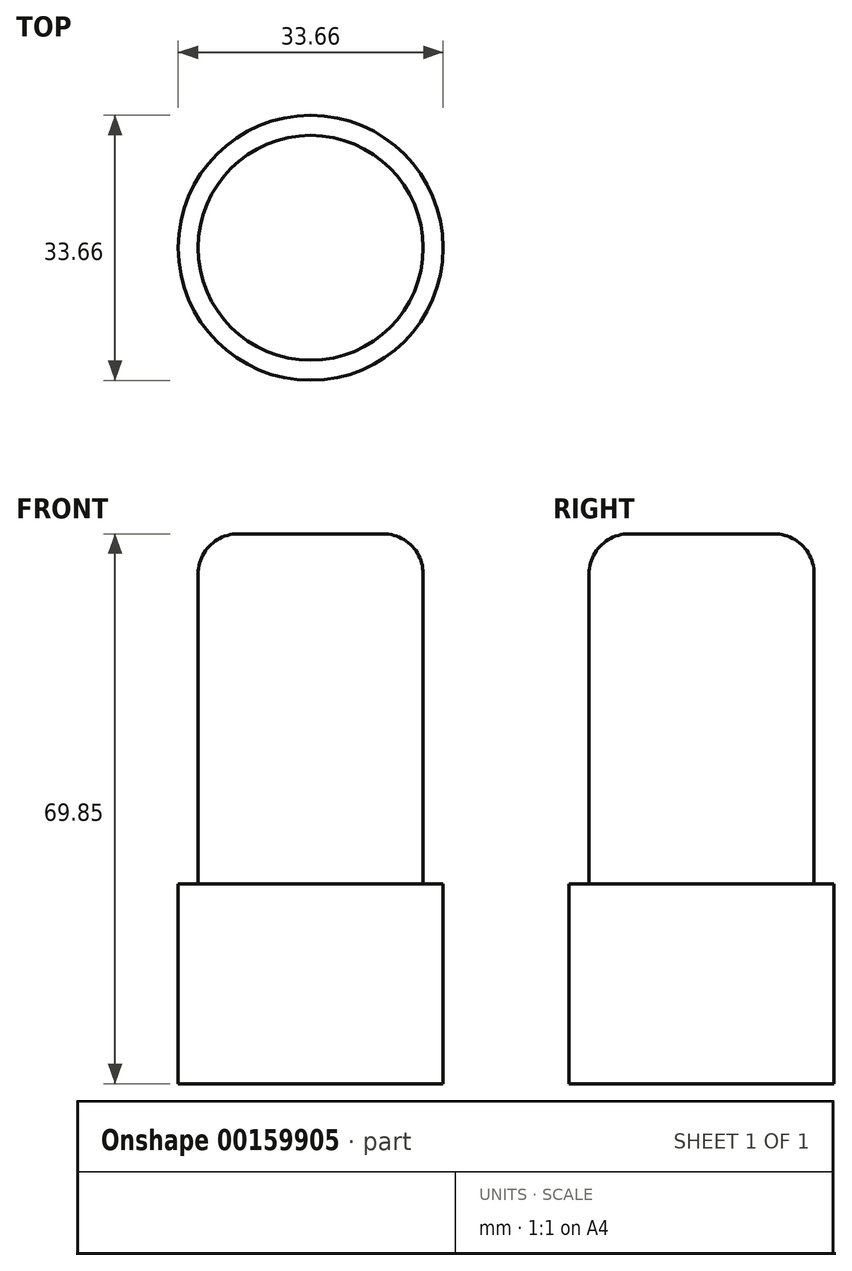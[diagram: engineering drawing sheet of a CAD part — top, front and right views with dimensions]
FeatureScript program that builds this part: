
annotation { "Feature Type Name" : "Feature", "Feature Type Description" : "" }
export const myFeature = defineFeature(function(context is Context, id is Id, definition is map)
    precondition{}
    {
        {
            var Q0;
            Q0=qCreatedBy(makeId("Top.planeOp"),FACE);
            var sketch = newSketch(context, id + "F0", { "sketchPlane" : qUnion([Q0])});
            skCircle(sketch, "E0", {"center": v(0, 0) * mm, "radius": 16.83 * mm});
            skSolve(sketch);
        }
        {
            var Q0;
            Q0=makeQuery(id+"F0.imprint","IMPRINT",FACE,{"disambiguationData":[TD([[makeQuery(id+"F0.imprint","IMPRINT",EDGE,{"derivedFrom":sQuery(id+"F0.wireOp",EDGE,"E0")}),1.0]])]});
            extrude(context, id + "F1", {"entities" : qUnion([Q0]), "depth" : 25.4 * mm});
        }
        {
            var Q0;
            Q0=makeQuery(id+"F1.opExtrude","CAP_FACE",FACE,{"disambiguationData":[OSD([sQuery(id+"F0.wireOp",EDGE,"E0")])],"isStart":false});
            var sketch = newSketch(context, id + "F2", { "sketchPlane" : qUnion([Q0])});
            skCircle(sketch, "E1", {"center": v(0, 0) * mm, "radius": 14.29 * mm});
            skSolve(sketch);
        }
        {
            var Q0;
            Q0 = qSketchRegion(id + "F2", true);
            extrude(context, id + "F3", {"entities" : qUnion([Q0]), "depth" : 44.45 * mm});
        }
        {
            var Q0;
            Q0=makeQuery(id+"F3.opExtrude","CAP_EDGE",EDGE,{"disambiguationData":[OSD([sQuery(id+"F2.wireOp",EDGE,"E1")])],"isStart":false});
            fillet(context, id + "F4", {"entities" : qUnion([Q0]), "radius" : 5.08 * mm, "tangentPropagation" : true, "allowEdgeOverflow" : false});
        }
    });
